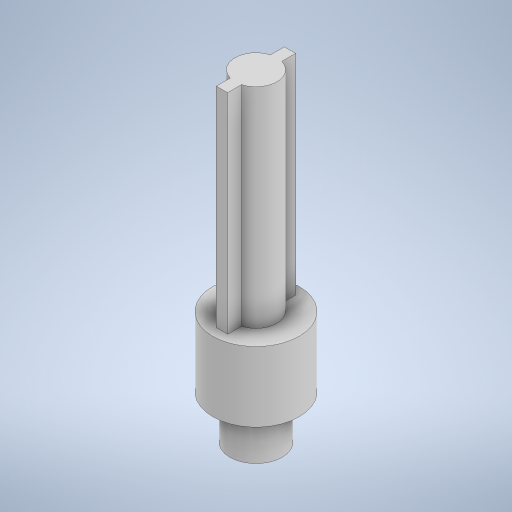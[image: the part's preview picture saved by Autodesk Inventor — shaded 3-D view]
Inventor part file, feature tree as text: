
AUTODESK INVENTOR PART (.ipt)
format: ipt  version: 2023 (Build 270158000, 158)  size: 273,920 bytes
history: native  units: in
note: dims shown in document units (in); Inventor stores cm internally (conversion verified against a paired STEP export)
features: extrude x4, sketch x4
ambient origin geometry x8: Origin, YZ Plane, XZ Plane, XY Plane, X Axis, Y Axis, Z Axis, Center Point
bodies: Solid1 (feature_tree)
feature tree (8):
  extrude  "Extrusion1"  Depth=0.315in TaperAngle=0.0deg
  extrude  "Extrusion2"  Depth=0.0512in
  extrude  "Extrusion3"  Depth=0.9449in TaperAngle=0.0deg
  extrude  "Extrusion6"  Depth=0.1969in TaperAngle=0.0deg
  sketch  "Sketch1"  dims[d0=0.3898in d1=0.315in d2=0.0in]
  sketch  "Sketch2"  dims[d3=0.189in d4=0.0512in]
  sketch  "Sketch3"  dims[d5=0.3071in d6=0.9449in d7=0.0in]
  sketch  "Sketch4"  dims[d8=0.2362in d9=0.1969in d10=0.0in d11=0.1378in d12=0.1024in d17=0.3937in d18=0.0in]
